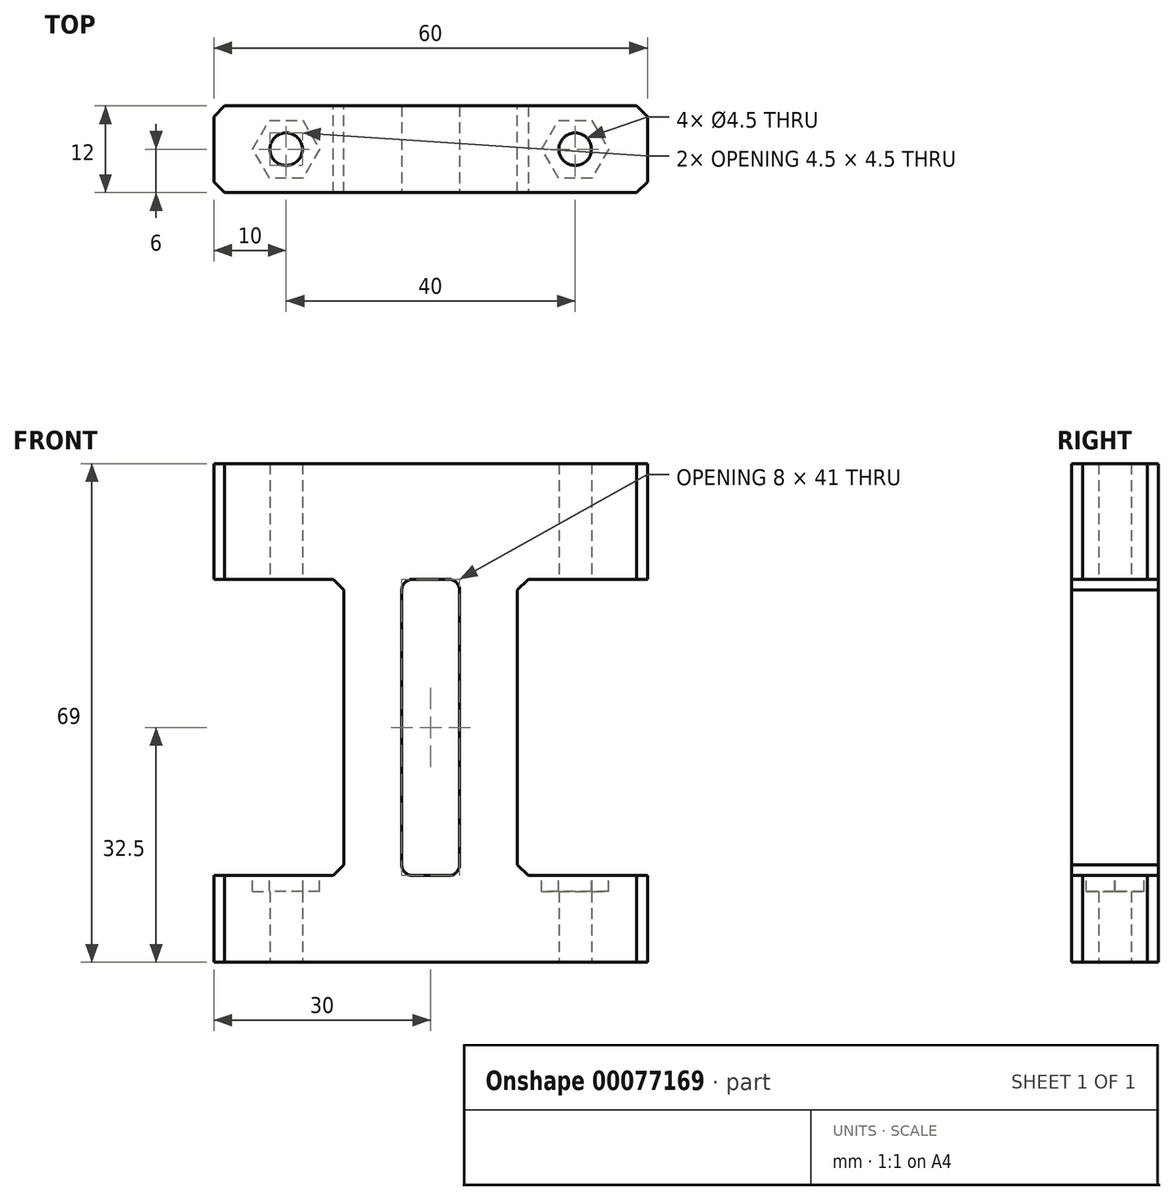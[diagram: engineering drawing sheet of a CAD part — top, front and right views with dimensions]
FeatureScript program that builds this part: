
annotation { "Feature Type Name" : "Feature", "Feature Type Description" : "" }
export const myFeature = defineFeature(function(context is Context, id is Id, definition is map)
    precondition{}
    {
        {
            var Q0;
            Q0=qCreatedBy(makeId("Front.planeOp"),FACE);
            var sketch = newSketch(context, id + "F0", { "sketchPlane" : qUnion([Q0])});
            skLineSegment(sketch, "E0.bottom", {"start": v(0, 0) * mm, "end": v(60, 0) * mm});
            skLineSegment(sketch, "E0.top", {"start": v(0, 69) * mm, "end": v(60, 69) * mm});
            skLineSegment(sketch, "E0.left", {"start": v(0, 0) * mm, "end": v(0, 12) * mm});
            skLineSegment(sketch, "E1.bottom", {"start": v(0, 53) * mm, "end": v(18, 53) * mm});
            skLineSegment(sketch, "E1.top", {"start": v(0, 12) * mm, "end": v(18, 12) * mm});
            skLineSegment(sketch, "E1.right", {"start": v(18, 53) * mm, "end": v(18, 12) * mm});
            skLineSegment(sketch, "E2.bottom", {"start": v(60, 12) * mm, "end": v(42, 12) * mm});
            skLineSegment(sketch, "E2.top", {"start": v(60, 53) * mm, "end": v(42, 53) * mm});
            skLineSegment(sketch, "E2.right", {"start": v(42, 12) * mm, "end": v(42, 53) * mm});
            skLineSegment(sketch, "E3.trimOffspring", {"start": v(0, 53) * mm, "end": v(0, 69) * mm});
            skLineSegment(sketch, "E4.trimOffspring", {"start": v(60, 53) * mm, "end": v(60, 69) * mm});
            skLineSegment(sketch, "E5", {"start": v(60, 12) * mm, "end": v(60, 0) * mm});
            skSolve(sketch);
        }
        {
            var Q0;
            Q0=qSketchRegion(id+"F0",true);
            extrude(context, id + "F1", {"entities" : qUnion([Q0]), "depth" : 12 * mm});
        }
        {
            var Q0;
            Q0=makeQuery(id+"F1.opExtrude","SWEPT_FACE",FACE,{"disambiguationData":[OSD([sQuery(id+"F0.wireOp",EDGE,"E0.bottom")])]});
            var sketch = newSketch(context, id + "F2", { "sketchPlane" : qUnion([Q0])});
            skCircle(sketch, "E6", {"center": v(10, 6) * mm, "radius": 2.25 * mm});
            skCircle(sketch, "E7", {"center": v(50, 6) * mm, "radius": 2.25 * mm});
            skSolve(sketch);
        }
        {
            var Q0;
            Q0=makeQuery(id+"F2.imprint","IMPRINT",FACE,{"disambiguationData":[TD([[makeQuery(id+"F2.imprint","IMPRINT",EDGE,{"derivedFrom":sQuery(id+"F2.wireOp",EDGE,"E6")}),1.0]])]});
            var Q1;
            Q1=makeQuery(id+"F2.imprint","IMPRINT",FACE,{"disambiguationData":[TD([[makeQuery(id+"F2.imprint","IMPRINT",EDGE,{"derivedFrom":sQuery(id+"F2.wireOp",EDGE,"E7")}),1.0]])]});
            extrude(context, id + "F3", {"entities" : qUnion([Q0, Q1]), "operationType" : NewBodyOperationType.REMOVE, "endBound" : BoundingType.UP_TO_NEXT, "oppositeDirection" : true, "depth" : 25 * mm});
        }
        {
            var Q0;
            Q0=makeQuery(id+"F1.opExtrude","CAP_EDGE",EDGE,{"disambiguationData":[OSD([sQuery(id+"F0.wireOp",EDGE,"E4.trimOffspring")])],"isStart":false});
            var Q1;
            Q1=makeQuery(id+"F1.opExtrude","CAP_EDGE",EDGE,{"disambiguationData":[OSD([sQuery(id+"F0.wireOp",EDGE,"E5")])],"isStart":false});
            var Q2;
            Q2=makeQuery(id+"F1.opExtrude","CAP_EDGE",EDGE,{"disambiguationData":[OSD([sQuery(id+"F0.wireOp",EDGE,"E5")])],"isStart":true});
            var Q3;
            Q3=makeQuery(id+"F1.opExtrude","CAP_EDGE",EDGE,{"disambiguationData":[OSD([sQuery(id+"F0.wireOp",EDGE,"E4.trimOffspring")])],"isStart":true});
            var Q4;
            Q4=makeQuery(id+"F1.opExtrude","CAP_EDGE",EDGE,{"disambiguationData":[OSD([sQuery(id+"F0.wireOp",EDGE,"E3.trimOffspring")])],"isStart":false});
            var Q5;
            Q5=makeQuery(id+"F1.opExtrude","CAP_EDGE",EDGE,{"disambiguationData":[OSD([sQuery(id+"F0.wireOp",EDGE,"E3.trimOffspring")])],"isStart":true});
            var Q6;
            Q6=makeQuery(id+"F1.opExtrude","CAP_EDGE",EDGE,{"disambiguationData":[OSD([sQuery(id+"F0.wireOp",EDGE,"E0.left")])],"isStart":true});
            var Q7;
            Q7=makeQuery(id+"F1.opExtrude","CAP_EDGE",EDGE,{"disambiguationData":[OSD([sQuery(id+"F0.wireOp",EDGE,"E0.left")])],"isStart":false});
            var Q8;
            Q8=makeQuery(id+"F1.opExtrude","SWEPT_EDGE",EDGE,{"disambiguationData":[OSD([sQuery(id+"F0.wireOp",EDGE,"E1.top"),sQuery(id+"F0.wireOp",EDGE,"E1.right")])]});
            var Q9;
            Q9=makeQuery(id+"F1.opExtrude","SWEPT_EDGE",EDGE,{"disambiguationData":[OSD([sQuery(id+"F0.wireOp",EDGE,"E1.bottom"),sQuery(id+"F0.wireOp",EDGE,"E1.right")])]});
            var Q10;
            Q10=makeQuery(id+"F1.opExtrude","SWEPT_EDGE",EDGE,{"disambiguationData":[OSD([sQuery(id+"F0.wireOp",EDGE,"E2.top"),sQuery(id+"F0.wireOp",EDGE,"E2.right")])]});
            var Q11;
            Q11=makeQuery(id+"F1.opExtrude","SWEPT_EDGE",EDGE,{"disambiguationData":[OSD([sQuery(id+"F0.wireOp",EDGE,"E2.bottom"),sQuery(id+"F0.wireOp",EDGE,"E2.right")])]});
            chamfer(context, id + "F4", {"entities" : qUnion([Q0, Q1, Q2, Q3, Q4, Q5, Q6, Q7, Q8, Q9, Q10, Q11]), "width" : 1.5 * mm, "tangentPropagation" : true});
        }
        {
            var Q0;
            Q0=makeQuery(id+"F1.opExtrude","CAP_FACE",FACE,{"disambiguationData":[OSD([sQuery(id+"F0.wireOp",EDGE,"E0.bottom"),sQuery(id+"F0.wireOp",EDGE,"E0.top"),sQuery(id+"F0.wireOp",EDGE,"E0.left"),sQuery(id+"F0.wireOp",EDGE,"E1.bottom"),sQuery(id+"F0.wireOp",EDGE,"E1.top"),sQuery(id+"F0.wireOp",EDGE,"E1.right"),sQuery(id+"F0.wireOp",EDGE,"E2.bottom"),sQuery(id+"F0.wireOp",EDGE,"E2.top"),sQuery(id+"F0.wireOp",EDGE,"E2.right"),sQuery(id+"F0.wireOp",EDGE,"E3.trimOffspring"),sQuery(id+"F0.wireOp",EDGE,"E4.trimOffspring"),sQuery(id+"F0.wireOp",EDGE,"E5")])],"isStart":false});
            var sketch = newSketch(context, id + "F5", { "sketchPlane" : qUnion([Q0])});
            skLineSegment(sketch, "E8.bottom", {"start": v(26, 53) * mm, "end": v(34, 53) * mm});
            skLineSegment(sketch, "E8.top", {"start": v(26, 12) * mm, "end": v(34, 12) * mm});
            skLineSegment(sketch, "E8.left", {"start": v(26, 53) * mm, "end": v(26, 12) * mm});
            skLineSegment(sketch, "E8.right", {"start": v(34, 53) * mm, "end": v(34, 12) * mm});
            skSolve(sketch);
        }
        {
            var Q0;
            Q0=qSketchRegion(id+"F5",true);
            extrude(context, id + "F6", {"entities" : qUnion([Q0]), "operationType" : NewBodyOperationType.REMOVE, "endBound" : BoundingType.THROUGH_ALL, "oppositeDirection" : true, "depth" : 25 * mm});
        }
        {
            var Q0;
            Q0=makeQuery(id+"F6.boolean.opBoolean","COPY",EDGE,{"derivedFrom":makeQuery(id+"F6.opExtrude","SWEPT_EDGE",EDGE,{"disambiguationData":[OSD([sQuery(id+"F5.wireOp",EDGE,"E8.bottom"),sQuery(id+"F5.wireOp",EDGE,"E8.left")])]})});
            var Q1;
            Q1=makeQuery(id+"F6.boolean.opBoolean","COPY",EDGE,{"derivedFrom":makeQuery(id+"F6.opExtrude","SWEPT_EDGE",EDGE,{"disambiguationData":[OSD([sQuery(id+"F5.wireOp",EDGE,"E8.bottom"),sQuery(id+"F5.wireOp",EDGE,"E8.right")])]})});
            var Q2;
            Q2=makeQuery(id+"F6.boolean.opBoolean","COPY",EDGE,{"derivedFrom":makeQuery(id+"F6.opExtrude","SWEPT_EDGE",EDGE,{"disambiguationData":[OSD([sQuery(id+"F5.wireOp",EDGE,"E8.top"),sQuery(id+"F5.wireOp",EDGE,"E8.right")])]})});
            var Q3;
            Q3=makeQuery(id+"F6.boolean.opBoolean","COPY",EDGE,{"derivedFrom":makeQuery(id+"F6.opExtrude","SWEPT_EDGE",EDGE,{"disambiguationData":[OSD([sQuery(id+"F5.wireOp",EDGE,"E8.top"),sQuery(id+"F5.wireOp",EDGE,"E8.left")])]})});
            fillet(context, id + "F7", {"entities" : qUnion([Q0, Q1, Q2, Q3]), "radius" : 1.5 * mm, "tangentPropagation" : true, "allowEdgeOverflow" : false});
        }
        {
            var Q0;
            Q0=makeQuery(id+"F1.opExtrude","SWEPT_FACE",FACE,{"disambiguationData":[OSD([sQuery(id+"F0.wireOp",EDGE,"E2.top")])]});
            var sketch = newSketch(context, id + "F8", { "sketchPlane" : qUnion([Q0])});
            skCircle(sketch, "E9", {"center": v(50, 6) * mm, "radius": 2.25 * mm});
            skCircle(sketch, "E10", {"center": v(10, 6) * mm, "radius": 2.25 * mm});
            skSolve(sketch);
        }
        {
            var Q0;
            Q0=qSketchRegion(id+"F8",true);
            extrude(context, id + "F9", {"entities" : qUnion([Q0]), "operationType" : NewBodyOperationType.REMOVE, "endBound" : BoundingType.UP_TO_NEXT, "oppositeDirection" : true, "depth" : 25 * mm});
        }
        {
            var Q0;
            Q0=makeQuery(id+"F1.opExtrude","SWEPT_FACE",FACE,{"disambiguationData":[OSD([sQuery(id+"F0.wireOp",EDGE,"E1.top")])]});
            var sketch = newSketch(context, id + "F10", { "sketchPlane" : qUnion([Q0])});
            skCircle(sketch, "E11.cCircle", {"center": v(10, -6) * mm, "radius": 4 * mm, "construction": true});
            skLineSegment(sketch, "E11.0", {"start": v(12.3, -10) * mm, "end": v(7.7, -10) * mm});
            skLineSegment(sketch, "E11.1", {"start": v(7.7, -10) * mm, "end": v(5.38, -6) * mm});
            skLineSegment(sketch, "E11.2", {"start": v(5.38, -6) * mm, "end": v(7.7, -2) * mm});
            skLineSegment(sketch, "E11.3", {"start": v(7.7, -2) * mm, "end": v(12.3, -2) * mm});
            skLineSegment(sketch, "E11.4", {"start": v(12.3, -2) * mm, "end": v(14.62, -6) * mm});
            skLineSegment(sketch, "E11.5", {"start": v(14.62, -6) * mm, "end": v(12.3, -10) * mm});
            skPoint(sketch, "E11.0.midPoint", {"position": v(10, -10) * mm});
            skCircle(sketch, "E12.cCircle", {"center": v(50, -6) * mm, "radius": 4 * mm, "construction": true});
            skLineSegment(sketch, "E12.0", {"start": v(54.62, -6) * mm, "end": v(52.31, -10) * mm});
            skLineSegment(sketch, "E12.1", {"start": v(52.31, -10) * mm, "end": v(47.7, -10) * mm});
            skLineSegment(sketch, "E12.2", {"start": v(47.7, -10) * mm, "end": v(45.38, -6) * mm});
            skLineSegment(sketch, "E12.3", {"start": v(45.38, -6) * mm, "end": v(47.69, -2) * mm});
            skLineSegment(sketch, "E12.4", {"start": v(47.69, -2) * mm, "end": v(52.3, -2) * mm});
            skLineSegment(sketch, "E12.5", {"start": v(52.3, -2) * mm, "end": v(54.62, -6) * mm});
            skPoint(sketch, "E12.0.midPoint", {"position": v(53.47, -8) * mm});
            skSolve(sketch);
        }
        {
            var Q0;
            Q0=qSketchRegion(id+"F10",true);
            extrude(context, id + "F11", {"entities" : qUnion([Q0]), "operationType" : NewBodyOperationType.REMOVE, "oppositeDirection" : true, "depth" : 2.2 * mm});
        }
    });
